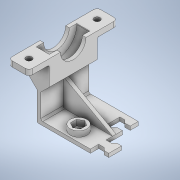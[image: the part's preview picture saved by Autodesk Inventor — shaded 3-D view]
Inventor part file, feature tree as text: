
AUTODESK INVENTOR PART (.ipt)
format: ipt  version: 2021 (Build 250183000, 183)  size: 302,080 bytes
history: native  units: mm
features: extrude x9, sketch x9, fillet x4, other x2, shell x1, chamfer x1, projected_geometry x1
ambient origin geometry x8: Origin, YZ Plane, XZ Plane, XY Plane, X Axis, Y Axis, Z Axis, Center Point
bodies: Body1 (feature_tree)
feature tree (27):
  other  "Твердое тело1"
  extrude  "Выдавливание1"  Depth=2.0mm
  extrude  "Выдавливание2"  Depth=20.0mm
  shell  "Оболочка1"  Thickness=2.0mm
  fillet  "Сопряжение1"  Radius=27.0mm
  extrude  "Выдавливание3"  Depth=26.1mm TaperAngle=0.0deg
  sketch  "Эскиз4"
  extrude  "Выдавливание4"  Depth=7.1mm
  extrude  "Выдавливание5"  Depth=22.1mm
  other  "Ребро жесткости1"
  extrude  "Выдавливание6"  Depth=2.0mm
  fillet  "Сопряжение2"  Radius=2.0mm
  fillet  "Сопряжение3"  Radius=13.5mm
  chamfer  "Фаска1"  Distance=2.0mm
  extrude  "Выдавливание7"  Depth=11.0mm
  extrude  "Выдавливание8"  Depth=14.0mm
  extrude  "Выдавливание9"  TaperAngle=0.0deg  [1 undecoded]
  fillet  "Сопряжение4"  Radius=3.0mm
  sketch  "Эскиз1"
  sketch  "Эскиз2"
  projected_geometry  "Спроецированная петля1"
  sketch  "Эскиз3"
  sketch  "Эскиз5"
  sketch  "Эскиз6"
  sketch  "Эскиз7"
  sketch  "Эскиз8"
  sketch  "Эскиз9"
note: 1 required parameter value undecoded (feature->parameter linkage not recoverable at this tier; creation-order binding heuristic only, values carry confidence <= 0.55)
